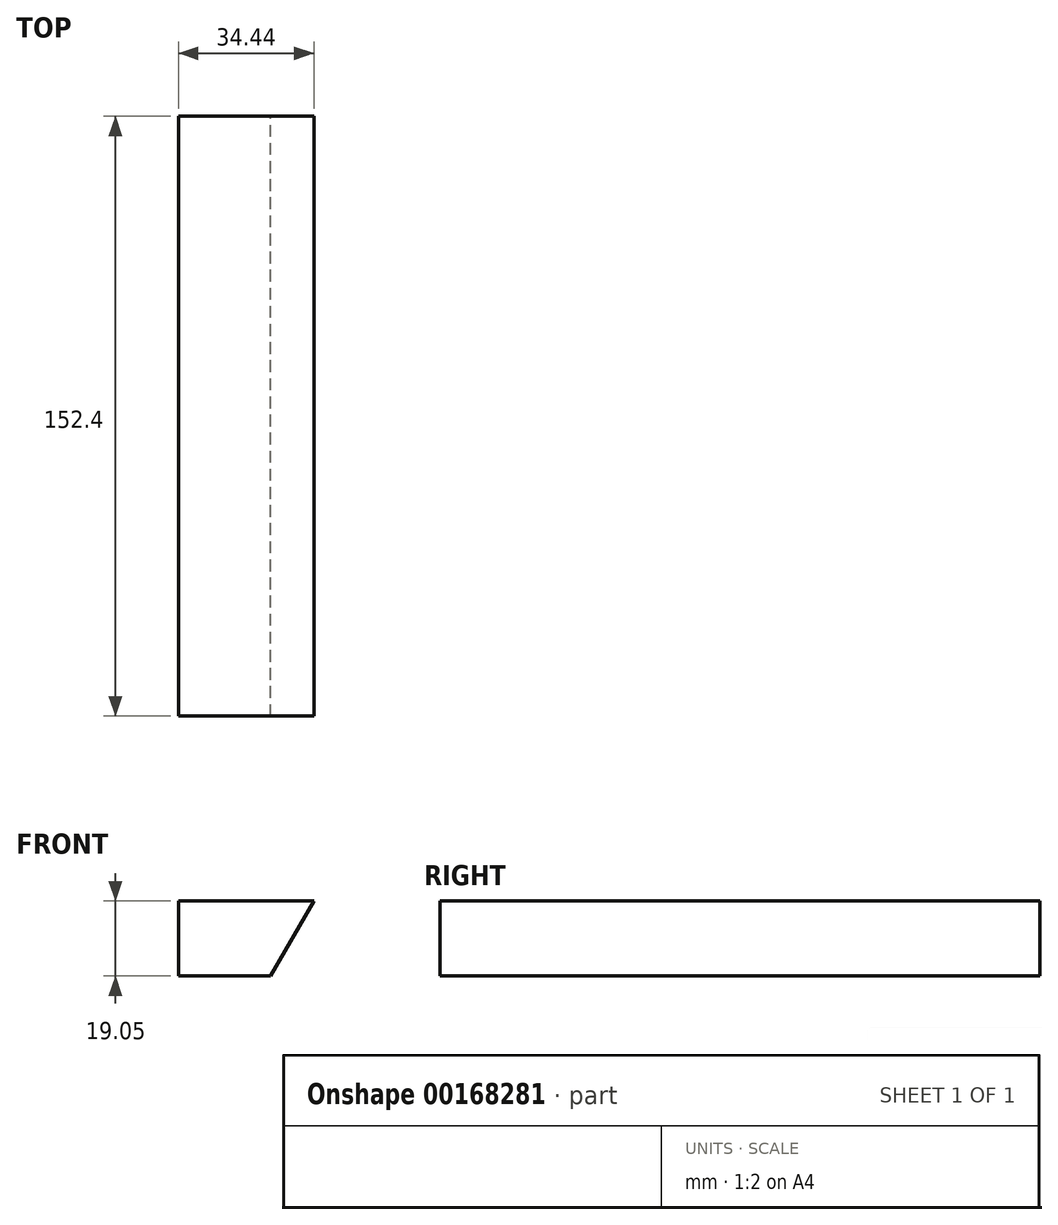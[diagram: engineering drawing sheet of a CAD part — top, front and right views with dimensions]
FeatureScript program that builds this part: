
annotation { "Feature Type Name" : "Feature", "Feature Type Description" : "" }
export const myFeature = defineFeature(function(context is Context, id is Id, definition is map)
    precondition{}
    {
        {
            var Q0;
            Q0=qCreatedBy(makeId("Front.planeOp"),FACE);
            var sketch = newSketch(context, id + "F0", { "sketchPlane" : qUnion([Q0])});
            skLineSegment(sketch, "E0", {"start": v(-23.81, 0) * mm, "end": v(10.63, 0) * mm});
            skLineSegment(sketch, "E1", {"start": v(10.63, 0) * mm, "end": v(10.63, 0) * mm});
            skLineSegment(sketch, "E2", {"start": v(10.63, 0) * mm, "end": v(-0.37, -19.05) * mm});
            skLineSegment(sketch, "E3", {"start": v(-23.81, 0) * mm, "end": v(-23.81, -38.1) * mm});
            skLineSegment(sketch, "E4", {"start": v(-23.81, -38.1) * mm, "end": v(-23.81, -38.1) * mm});
            skLineSegment(sketch, "E5", {"start": v(21.63, -19.05) * mm, "end": v(32.62, 0) * mm});
            skLineSegment(sketch, "E6", {"start": v(32.62, 0) * mm, "end": v(47.03, 0) * mm});
            skLineSegment(sketch, "E7", {"start": v(47.03, 0) * mm, "end": v(47.03, -19.05) * mm});
            skLineSegment(sketch, "E8", {"start": v(-0.37, -19.05) * mm, "end": v(52.39, -19.05) * mm});
            skLineSegment(sketch, "E9", {"start": v(52.39, -19.05) * mm, "end": v(52.39, -38.1) * mm});
            skPoint(sketch, "E10.orphan", {"position": v(0, -19.05) * mm});
            skPoint(sketch, "E11.start.orphan", {"position": v(0, -18.4) * mm});
            skLineSegment(sketch, "E12", {"start": v(-23.81, -38.1) * mm, "end": v(52.39, -38.1) * mm});
            skSolve(sketch);
        }
        {
            var Q0;
            Q0=qCreatedBy(makeId("Front.planeOp"),FACE);
            var sketch = newSketch(context, id + "F1", { "sketchPlane" : qUnion([Q0])});
            skLineSegment(sketch, "E13.0", {"start": v(-23.81, 0) * mm, "end": v(10.63, 0) * mm});
            skLineSegment(sketch, "E14.0", {"start": v(10.63, 0) * mm, "end": v(-0.37, -19.05) * mm});
            skLineSegment(sketch, "E15.0", {"start": v(-23.81, 0) * mm, "end": v(-23.81, -19.05) * mm});
            skLineSegment(sketch, "E16", {"start": v(-0.37, -19.05) * mm, "end": v(-23.81, -19.05) * mm});
            skPoint(sketch, "E17.orphan", {"position": v(-23.81, -38.1) * mm});
            skSolve(sketch);
        }
        {
            var Q0;
            Q0=qSketchRegion(id+"F1",true);
            extrude(context, id + "F2", {"entities" : qUnion([Q0]), "depth" : 152.4 * mm});
        }
    });
